# Revit family: Shower_Valve-Thermostat-Grohe-Grohtherm_1000-34150003
name_source: partatom
category: Plumbing Fixtures
revit_build: Autodesk Revit 2018 (Build: 20170223_1515(x64)
units: mm (PartAtom-declared; Revit-internal decimal feet)

## family parameters
Cut with Voids When Loaded = No
Host = Face
Part Type = Normal
Room Calculation Point = No
Round Connector Dimension = Use Diameter
Shared = Yes

## types (1)
- 34521001
    Assembly Code = D2010710
    CW Connection = Yes
    CWFU = 3
    Cold Water Connection Diameter = 1/2"
    Default Elevation = 0"
    Description = Grohtherm 1000 Thermostatic Shower Valve: GROHE CoolTouch safety housing, GROHE MetalGrip ergonomically shaped metal handles, exposed thermostatic temperature control with SafeStop at 100°F/38°C, GROHE TurboStat Compact cartridge with wax thermoelement, integrated mixed water shut off, volume control handle with economy button and individually adjustable economy stop, 1/2" ceramic cartridge (180° turn), 1/2" Shower bottom outlet, built-in non-return valves, dirt strainers, backflow protected, S-union 1/2" NPT, metal escutcheon and GROHE EcoJoy technology for less water and perfect flow.
    Finish = Metal-Grohe-000-StarLight Chrome
    HW Connection = Yes
    HWFU = 3
    Hot Water Connection Diameter = 1/2"
    IAPMO Compliance = ASME A112.18.1/CSA B125.1
    Installation Type = Wall Mounted
    Manufacturer = Grohe
    Material = Metal-Grohe-000-StarLight Chrome
    Min. Recommended Pressure = 15 psi (1.0 bar)
    Model = 34521001
    Price = Prices may vary. Please consult Manufacturer Representative for most up-to-date price list.
    Product Documentation Link = https://americanstandard.box.com
    Product Page URL = https://www.grohe.us
    Revised Date = 07/22/2021
    Tempered Water Connection = Yes
    Tempered Water Connection Diameter = 1/2"
    URL = https://www.grohe.us
    Vent Connection = No
    WFU = 4
    Waste Connection = No
    Width = 12 1/2"

## geometry (parser evidence)
native form markers: Sweep x2
no freeform markers — native parametric forms only
